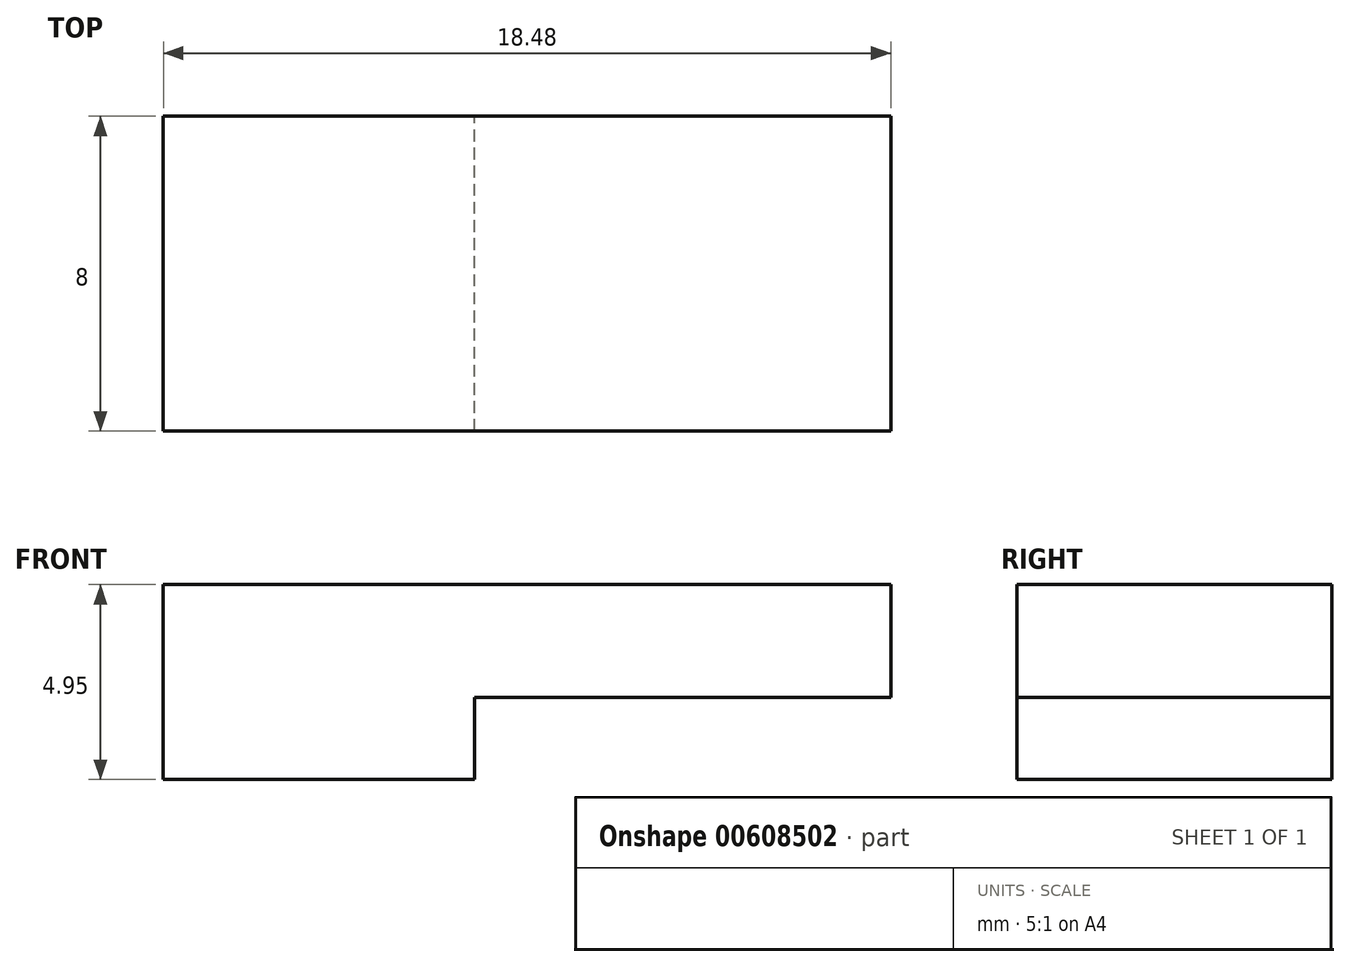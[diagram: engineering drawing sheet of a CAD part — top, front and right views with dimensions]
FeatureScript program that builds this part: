
annotation { "Feature Type Name" : "Feature", "Feature Type Description" : "" }
export const myFeature = defineFeature(function(context is Context, id is Id, definition is map)
    precondition{}
    {
        {
            var Q0;
            Q0=qCreatedBy(makeId("Front.planeOp"),FACE);
            var sketch = newSketch(context, id + "F0", { "sketchPlane" : qUnion([Q0])});
            skLineSegment(sketch, "E0.bottom", {"start": v(-7.91, 0) * mm, "end": v(0, 0) * mm});
            skLineSegment(sketch, "E0.top", {"start": v(-7.91, 2.08) * mm, "end": v(0, 2.08) * mm});
            skLineSegment(sketch, "E0.left", {"start": v(-7.91, 0) * mm, "end": v(-7.91, 2.08) * mm});
            skLineSegment(sketch, "E0.right", {"start": v(0, 0) * mm, "end": v(0, 2.08) * mm});
            skLineSegment(sketch, "E1.bottom", {"start": v(-7.91, 2.08) * mm, "end": v(10.57, 2.08) * mm});
            skLineSegment(sketch, "E1.top", {"start": v(-7.91, 4.95) * mm, "end": v(10.57, 4.95) * mm});
            skLineSegment(sketch, "E1.left", {"start": v(-7.91, 2.08) * mm, "end": v(-7.91, 4.95) * mm});
            skLineSegment(sketch, "E1.right", {"start": v(10.57, 2.08) * mm, "end": v(10.57, 4.95) * mm});
            skSolve(sketch);
        }
        {
            var Q0;
            Q0=makeQuery(id+"F0.imprint","IMPRINT",FACE,{"disambiguationData":[TD([[makeQuery(id+"F0.imprint","IMPRINT",EDGE,{"derivedFrom":sQuery(id+"F0.wireOp",EDGE,"E1.top")}),-1.0]])]});
            var Q1;
            Q1=makeQuery(id+"F0.imprint","IMPRINT",FACE,{"disambiguationData":[TD([[makeQuery(id+"F0.imprint","IMPRINT",EDGE,{"derivedFrom":sQuery(id+"F0.wireOp",EDGE,"E0.bottom")}),1.0]])]});
            var Q2;
            Q2 = qConstructionFilter(qBodyType(qCreatedBy(id + "F0" ,EDGE), BodyType.WIRE), ConstructionObject.NO);
            extrude(context, id + "F1", {"entities" : qUnion([Q0, Q1]), "surfaceEntities" : qUnion([Q2]), "depth" : 8 * mm, "offsetDistance" : 25 * mm});
        }
    });
